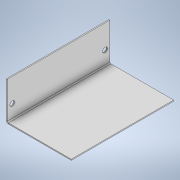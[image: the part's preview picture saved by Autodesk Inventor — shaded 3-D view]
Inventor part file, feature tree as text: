
AUTODESK INVENTOR PART (.ipt)
format: ipt  version: 2022 (Build 260153000, 153)  size: 143,360 bytes
history: native  units: in
note: dims shown in document units (in); Inventor stores cm internally (conversion verified against a paired STEP export)
features: other x4, sketch x4, hole x2
ambient origin geometry x8: Origin, YZ Plane, XZ Plane, XY Plane, X Axis, Y Axis, Z Axis, Center Point
bodies: Body1 (feature_tree)
feature tree (10):
  other  "Sólido1"
  other  "Cara1"
  other  "Pliegue1"
  hole  "Agujero3"  [1 undecoded]
  hole  "Agujero4"  [1 undecoded]
  sketch  "Boceto1"  dims[d0=3.7795in d1=3.7402in]
  other  "Placa1"
  sketch  "Boceto4"  dims[d2=0.0394in d3=2.3622in]
  sketch  "Boceto7"  dims[d4=2.3622in]
  sketch  "Boceto8"  dims[d5=0.0394in d6=0.0197in d7=0.0787in d8=0.0394in d9=90.0deg d10=0.0394in d11=0.1772in d12=0.4724in d13=0.1772in d14=0.1772in d15=0.4724in d16=0.1772in d24=0.1772in d25=0.4724in d26=0.1772in d36=0.861in d37=0.1772in d38=0.1772in d39=0.2362in d40=0.1575in d41=0.0787in d42=90.0deg d43=0.315in d44=0.8108in d45=0.861in d46=0.1772in d47=0.1772in d48=0.2362in d49=0.1575in d50=0.0787in d51=90.0deg d52=0.315in d53=0.8108in]
note: 2 required parameter values undecoded (feature->parameter linkage not recoverable at this tier; creation-order binding heuristic only, values carry confidence <= 0.55)
